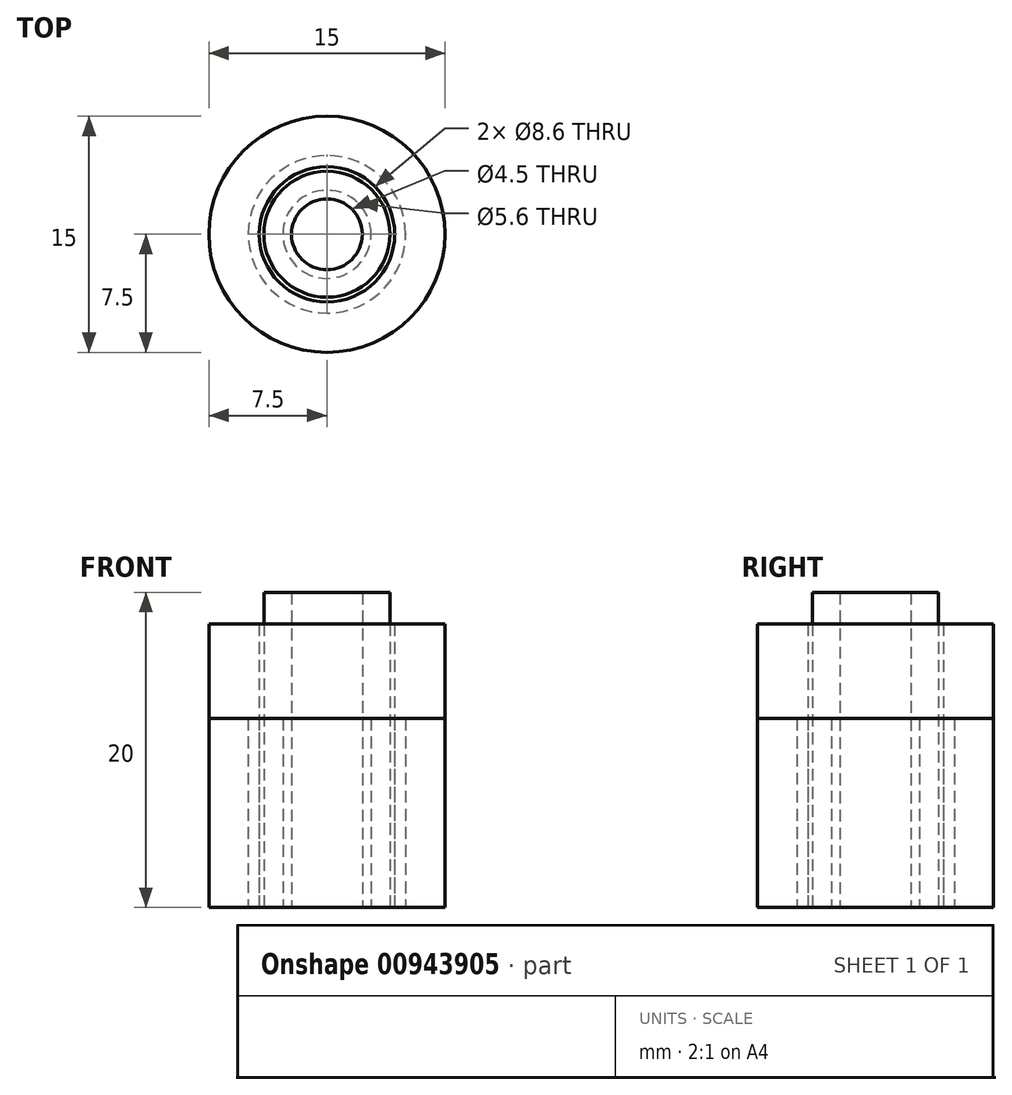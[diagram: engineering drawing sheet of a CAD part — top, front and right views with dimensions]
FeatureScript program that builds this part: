
annotation { "Feature Type Name" : "Feature", "Feature Type Description" : "" }
export const myFeature = defineFeature(function(context is Context, id is Id, definition is map)
    precondition{}
    {
        {
            var Q0;
            Q0=qCreatedBy(makeId("Top.planeOp"),FACE);
            var sketch = newSketch(context, id + "F0", { "sketchPlane" : qUnion([Q0])});
            skCircle(sketch, "E0", {"center": v(0, 0) * mm, "radius": 5 * mm});
            skCircle(sketch, "E1", {"center": v(0, 0) * mm, "radius": 2.8 * mm});
            skSolve(sketch);
        }
        {
            var Q0;
            Q0=makeQuery(id+"F0.imprint","IMPRINT",FACE,{"disambiguationData":[TD([[makeQuery(id+"F0.imprint","IMPRINT",EDGE,{"derivedFrom":sQuery(id+"F0.wireOp",EDGE,"E0")}),1.0]])]});
            extrude(context, id + "F1", {"entities" : qUnion([Q0]), "depth" : 12 * mm, "offsetDistance" : 25 * mm});
        }
        {
            var Q0;
            Q0=qCreatedBy(makeId("Top.planeOp"),FACE);
            var sketch = newSketch(context, id + "F2", { "sketchPlane" : qUnion([Q0])});
            skCircle(sketch, "E2", {"center": v(0, 0) * mm, "radius": 4.3 * mm});
            skCircle(sketch, "E3", {"center": v(0, 0) * mm, "radius": 7.5 * mm});
            skSolve(sketch);
        }
        {
            var Q0;
            Q0=makeQuery(id+"F2.imprint","IMPRINT",FACE,{"disambiguationData":[TD([[makeQuery(id+"F2.imprint","IMPRINT",EDGE,{"derivedFrom":sQuery(id+"F2.wireOp",EDGE,"E2")}),-1.0]])]});
            extrude(context, id + "F3", {"entities" : qUnion([Q0]), "depth" : 18 * mm, "offsetDistance" : 25 * mm});
        }
        {
            var Q0;
            Q0=qCreatedBy(makeId("Top.planeOp"),FACE);
            var sketch = newSketch(context, id + "F4", { "sketchPlane" : qUnion([Q0])});
            skCircle(sketch, "E4", {"center": v(0, 0) * mm, "radius": 4.3 * mm});
            skCircle(sketch, "E5", {"center": v(0, 0) * mm, "radius": 7.5 * mm});
            skSolve(sketch);
        }
        {
            var Q0;
            Q0 = qSketchRegion(id + "F4", true);
            extrude(context, id + "F5", {"entities" : qUnion([Q0]), "depth" : 12 * mm, "offsetDistance" : 25 * mm});
        }
        {
            var Q0;
            Q0=qCreatedBy(makeId("Top.planeOp"),FACE);
            var sketch = newSketch(context, id + "F6", { "sketchPlane" : qUnion([Q0])});
            skCircle(sketch, "E6", {"center": v(0, 0) * mm, "radius": 2.25 * mm});
            skCircle(sketch, "E7", {"center": v(0, 0) * mm, "radius": 4 * mm});
            skSolve(sketch);
        }
        {
            var Q0;
            Q0=makeQuery(id+"F6.imprint","IMPRINT",FACE,{"disambiguationData":[TD([[makeQuery(id+"F6.imprint","IMPRINT",EDGE,{"derivedFrom":sQuery(id+"F6.wireOp",EDGE,"E6")}),-1.0]])]});
            extrude(context, id + "F7", {"entities" : qUnion([Q0]), "depth" : 20 * mm, "offsetDistance" : 25 * mm});
        }
    });
